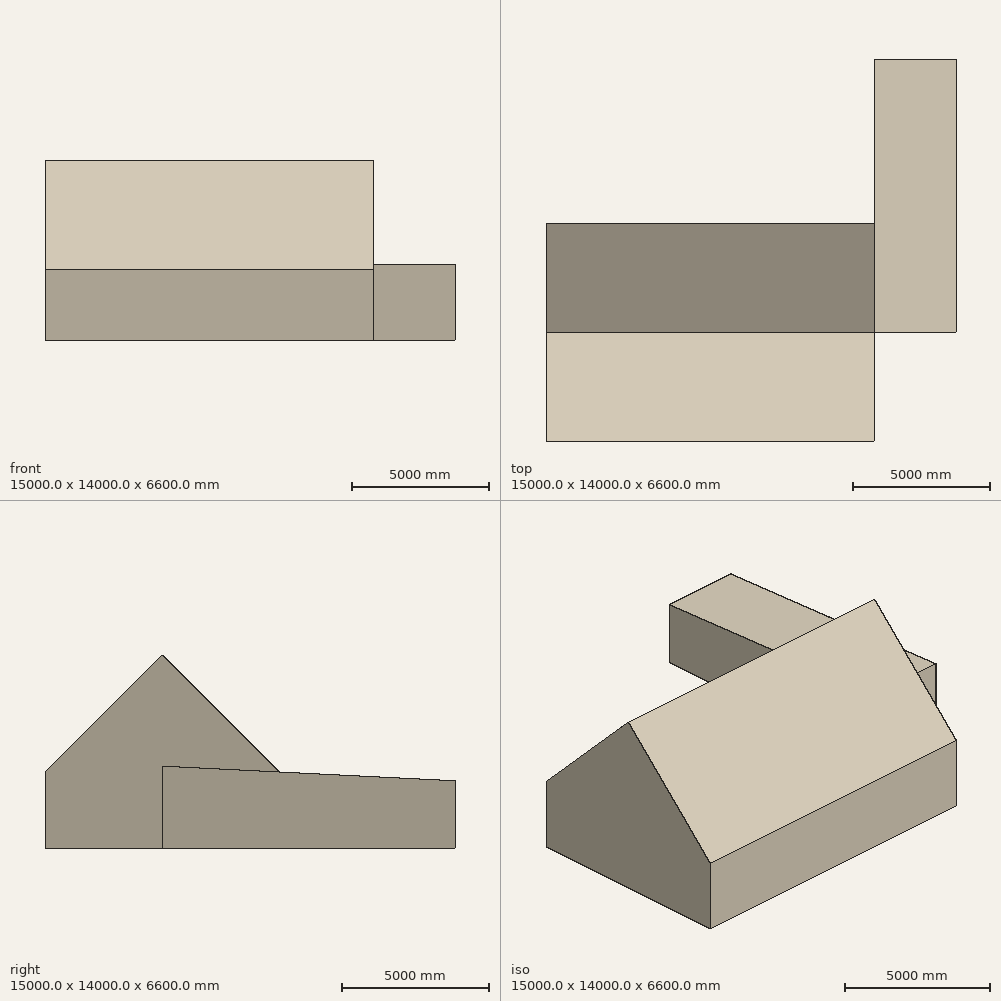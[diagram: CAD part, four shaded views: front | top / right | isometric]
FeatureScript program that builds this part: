
annotation { "Feature Type Name" : "Feature", "Feature Type Description" : "" }
export const myFeature = defineFeature(function(context is Context, id is Id, definition is map)
    precondition{}
    {
        {
            var Q0;
            Q0=qCreatedBy(makeId("Top.planeOp"),FACE);
            var sketch = newSketch(context, id + "F0", { "sketchPlane" : qUnion([Q0])});
            skLineSegment(sketch, "E0", {"start": v(-6006.6, -1566.58) * mm, "end": v(5993.4, -1566.58) * mm});
            skLineSegment(sketch, "E1", {"start": v(5993.4, -1566.58) * mm, "end": v(5993.4, 6433.42) * mm});
            skLineSegment(sketch, "E2", {"start": v(-6006.6, -1566.58) * mm, "end": v(-6006.6, 6433.42) * mm});
            skLineSegment(sketch, "E3", {"start": v(-6006.6, 6433.42) * mm, "end": v(5993.4, 6433.42) * mm});
            skPoint(sketch, "E4.end.orphan", {"position": v(5993.4, 12433.42) * mm});
            skPoint(sketch, "E5.end.orphan", {"position": v(5993.4, 2433.42) * mm});
            skPoint(sketch, "E6", {"position": v(-6006.6, 2433.42) * mm});
            skSolve(sketch);
        }
        {
            var Q0;
            Q0 = qSketchRegion(id + "F0", true);
            extrude(context, id + "F1", {"entities" : qUnion([Q0]), "depth" : 2600 * mm});
        }
        {
            var Q0;
            Q0=makeQuery(id+"F1.opExtrude","SWEPT_FACE",FACE,{"disambiguationData":[OSD([sQuery(id+"F0.wireOp",EDGE,"E2")])]});
            var sketch = newSketch(context, id + "F2", { "sketchPlane" : qUnion([Q0])});
            skLineSegment(sketch, "E7", {"start": v(-6433.42, 2600) * mm, "end": v(1566.58, 2600) * mm});
            skLineSegment(sketch, "E8", {"start": v(-2433.42, 6600) * mm, "end": v(-6433.42, 2600) * mm});
            skLineSegment(sketch, "E9", {"start": v(-2433.42, 6600) * mm, "end": v(1566.58, 2600) * mm});
            skPoint(sketch, "E10.start.orphan", {"position": v(-2433.42, 2600) * mm});
            skSolve(sketch);
        }
        {
            var Q0;
            Q0 = qSketchRegion(id + "F2", true);
            extrude(context, id + "F3", {"entities" : qUnion([Q0]), "operationType" : NewBodyOperationType.ADD, "oppositeDirection" : true, "depth" : 12000 * mm});
        }
        {
            var Q0;
            Q0=makeQuery(id+"F3.boolean.opBoolean","MERGE",FACE,{"derivedFrom":[makeQuery(id+"F1.opExtrude","SWEPT_FACE",FACE,{"disambiguationData":[OSD([sQuery(id+"F0.wireOp",EDGE,"E1")])]}),makeQuery(id+"F3.opExtrude","CAP_FACE",FACE,{"disambiguationData":[OSD([sQuery(id+"F2.wireOp",EDGE,"E7"),sQuery(id+"F2.wireOp",EDGE,"E8"),sQuery(id+"F2.wireOp",EDGE,"E9")])],"isStart":false})]});
            var sketch = newSketch(context, id + "F4", { "sketchPlane" : qUnion([Q0])});
            skLineSegment(sketch, "E11", {"start": v(2433.42, 0) * mm, "end": v(12433.42, 0) * mm});
            skLineSegment(sketch, "E12", {"start": v(2433.42, 0) * mm, "end": v(2433.42, 2800) * mm});
            skPoint(sketch, "E13.end.orphan", {"position": v(12433.42, 2800) * mm});
            skLineSegment(sketch, "E14", {"start": v(12433.42, 0) * mm, "end": v(12433.42, 2300) * mm});
            skLineSegment(sketch, "E15", {"start": v(2433.42, 2800) * mm, "end": v(12433.42, 2300) * mm});
            skSolve(sketch);
        }
        {
            var Q0;
            Q0 = qSketchRegion(id + "F4", true);
            extrude(context, id + "F5", {"entities" : qUnion([Q0]), "operationType" : NewBodyOperationType.ADD, "depth" : 3000 * mm});
        }
    });
